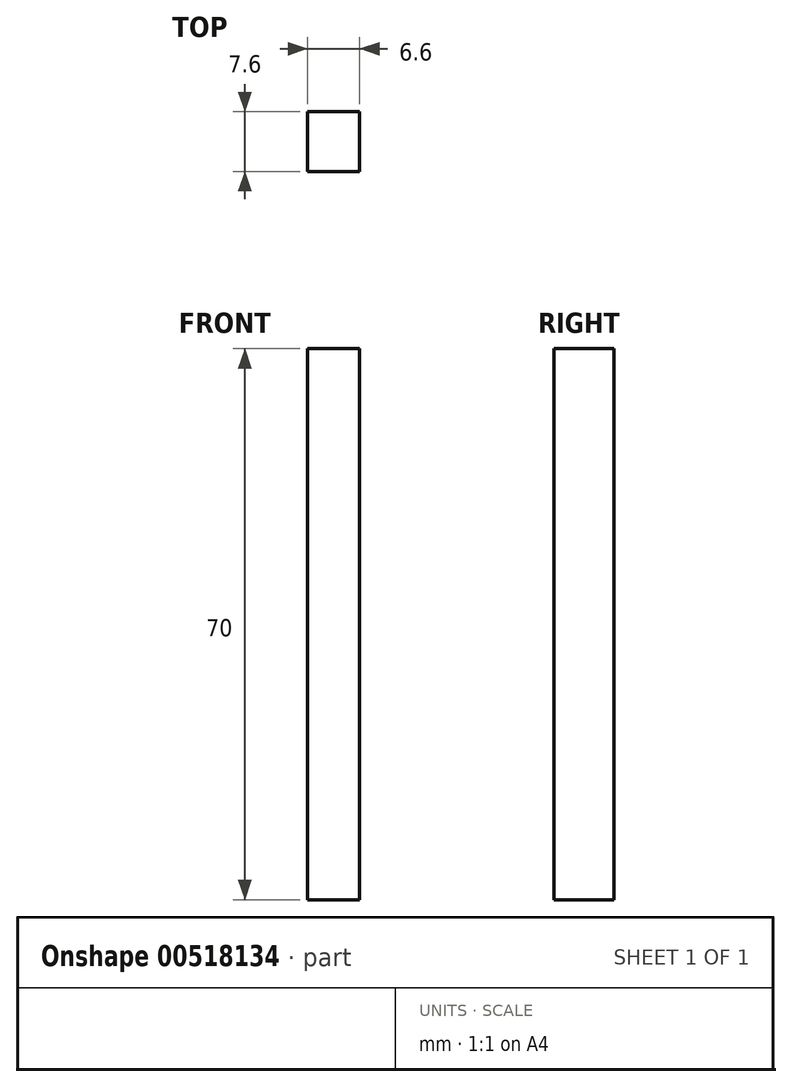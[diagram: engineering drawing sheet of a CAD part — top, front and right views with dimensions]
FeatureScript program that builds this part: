
annotation { "Feature Type Name" : "Feature", "Feature Type Description" : "" }
export const myFeature = defineFeature(function(context is Context, id is Id, definition is map)
    precondition{}
    {
        {
            var Q0;
            Q0=qCreatedBy(makeId("Top.planeOp"),FACE);
            var sketch = newSketch(context, id + "F0", { "sketchPlane" : qUnion([Q0])});
            skLineSegment(sketch, "E0.bottom", {"start": v(0, 0) * mm, "end": v(-6.6, 0) * mm});
            skLineSegment(sketch, "E0.top", {"start": v(0, -7.6) * mm, "end": v(-6.6, -7.6) * mm});
            skLineSegment(sketch, "E0.left", {"start": v(0, 0) * mm, "end": v(0, -7.6) * mm});
            skLineSegment(sketch, "E0.right", {"start": v(-6.6, 0) * mm, "end": v(-6.6, -7.6) * mm});
            skSolve(sketch);
        }
        {
            var Q0;
            Q0 = qSketchRegion(id + "F0", true);
            extrude(context, id + "F1", {"entities" : qUnion([Q0]), "depth" : 70 * mm, "offsetDistance" : 25 * mm});
        }
    });
